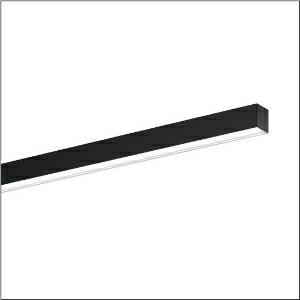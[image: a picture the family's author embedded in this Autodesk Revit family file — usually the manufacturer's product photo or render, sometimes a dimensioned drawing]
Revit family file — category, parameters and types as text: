
# Revit family: silica_r__21_51mx20tct5b_b82d
name_source: partatom
category: Lighting Fixtures
units: mm (PartAtom-declared; Revit-internal decimal feet)

## family parameters
Cut with Voids When Loaded = No
Host = Face
Light Source = No
Part Type = Normal
Room Calculation Point = No
Round Connector Dimension = Use Diameter
Shared = No

## types (1)
- --- (1 x LED, 6000 lm, 51.3 W, 6500K)
    Apparent Load = 51 VA
    CIE Flux Codes = 48 79 96 100 100
    Color Rendering = 80
    Color Temperature = 6500K
    Default Elevation = 1800 mm
    Description = Silica® 21, office luminaire, primary optical cover: cover, of PMMA, opal, light emission: direct distribution, primary light characteristic: symmetric, installation type: surface-mounted, LED, rated luminous flux: 6.000lm, luminous efficacy: 112lm/W, light colour: 8tw, colour temperature: 2700..6500K, control gear: DALI DT8, with terminal, 3+2-pole, max. 2.5mm², mains connection: 220..240V, AC, 50/60Hz, rated input power: 53.8W, luminaire housing, of aluminium, matt jet black (RAL 9005), length: 3.004mm, width: 53mm, height: 53mm, protection rating (complete): IP20, insulation class (complete): insulation class I (protective earthing), certification: CE, permissible operating ambient temperature: 0..+35°C, standard: EN 50419, packaging unit: 1 piece
    Height = 53 mm
    Lamp = 1 x LED
    Lamp Light Flux = 6000 lm
    Lamp Power = 51.3 W
    Lamp count = 1
    Length = 3004 mm
    Luminous efficacy = 117 lm/W
    Manufacturer = Siteco
    ModVariant = No
    Model = 51MX20TCT5B
    Mounting Place = Ceiling
    Mounting Type = Surface mounted
    Number of Poles = 1
    OnlyDefault = Yes
    Power Factor = 1
    Product Name = Silica® 21
    Product group = office luminaire | ceiling mounted
    ProductGroupID = 303
    Protection Class = Protection class I
    Protection Degree = IP 20
    RLX_Detail_Level = 1
    RLX_Emergency_Light_Flux = 0 lm
    RLX_Emergency_Type = 0
    RLX_Emergency_Type_DB = No
    RlxData = <blob elided: 25581 chars, md5=a3a8bb01>
    Socket = socket
    Standby Power = 0 W
    System Light Flux = 6000 lm
    System Power = 51 W
    Type Comments = individual setting
    Type Image = l_1335925.jpg
    URL = http://relux.com
    VarID = @adj_161159
    Voltage = 0 V
    Weight = 0.00 kg
    Width = 53 mm

## geometry (parser evidence)
native form markers: Blend x4, Sweep x11
no freeform markers — native parametric forms only
